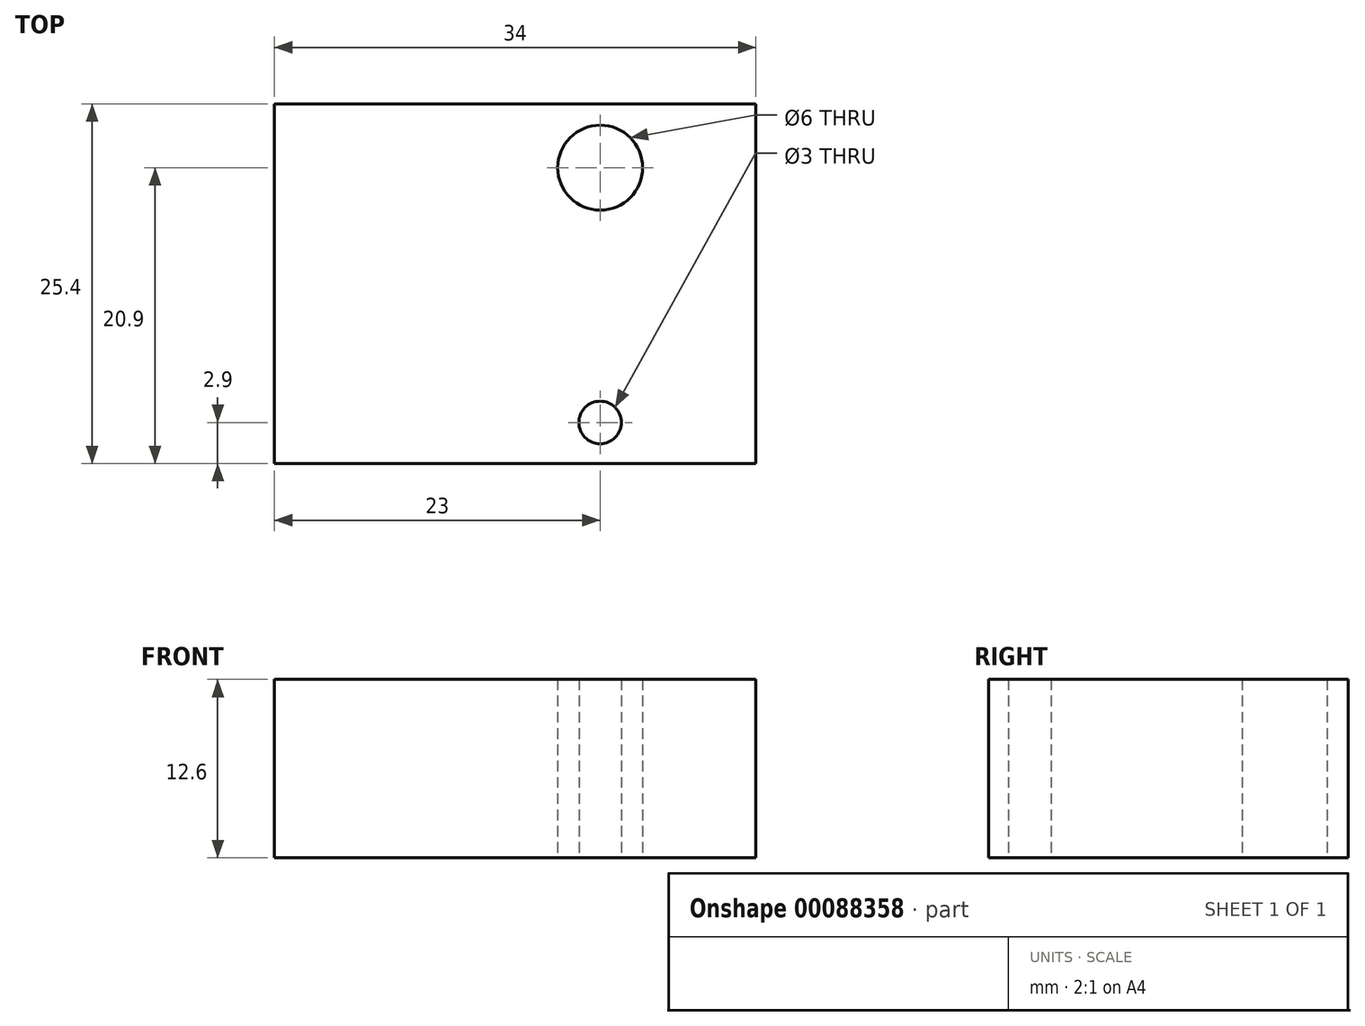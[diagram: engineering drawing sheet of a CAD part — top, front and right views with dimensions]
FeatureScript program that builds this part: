
annotation { "Feature Type Name" : "Feature", "Feature Type Description" : "" }
export const myFeature = defineFeature(function(context is Context, id is Id, definition is map)
    precondition{}
    {
        {
            var Q0;
            Q0=qCreatedBy(makeId("Top.planeOp"),FACE);
            var sketch = newSketch(context, id + "F0", { "sketchPlane" : qUnion([Q0])});
            skLineSegment(sketch, "E0.bottom", {"start": v(17, -12.7) * mm, "end": v(-17, -12.7) * mm});
            skLineSegment(sketch, "E0.top", {"start": v(17, 12.7) * mm, "end": v(-17, 12.7) * mm});
            skLineSegment(sketch, "E0.left", {"start": v(17, -12.7) * mm, "end": v(17, 12.7) * mm});
            skLineSegment(sketch, "E0.right", {"start": v(-17, -12.7) * mm, "end": v(-17, 12.7) * mm});
            skPoint(sketch, "E0.middle", {"position": v(0, 0) * mm});
            skCircle(sketch, "E1", {"center": v(6, 8.2) * mm, "radius": 3 * mm});
            skCircle(sketch, "E2", {"center": v(6, -9.8) * mm, "radius": 1.5 * mm});
            skSolve(sketch);
        }
        {
            var Q0;
            Q0 = qSketchRegion(id + "F0", true);
            extrude(context, id + "F1", {"entities" : qUnion([Q0]), "depth" : 12.6 * mm});
        }
    });
